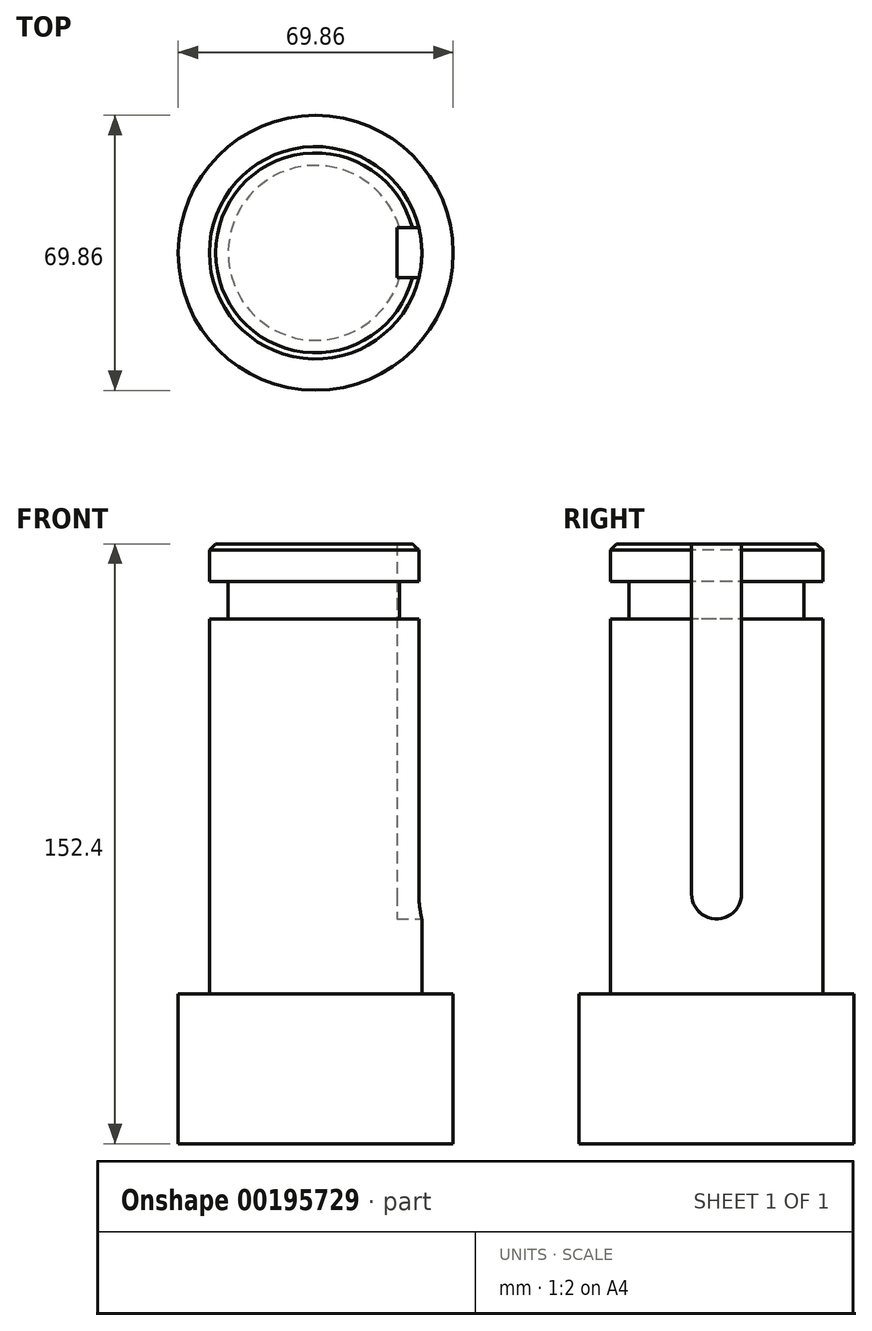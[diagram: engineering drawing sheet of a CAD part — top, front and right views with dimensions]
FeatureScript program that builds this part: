
annotation { "Feature Type Name" : "Feature", "Feature Type Description" : "" }
export const myFeature = defineFeature(function(context is Context, id is Id, definition is map)
    precondition{}
    {
        {
            var Q0;
            Q0=qCreatedBy(makeId("Top.planeOp"),FACE);
            var sketch = newSketch(context, id + "F0", { "sketchPlane" : qUnion([Q0])});
            skCircle(sketch, "E0", {"center": v(0, 0) * mm, "radius": 26.99 * mm});
            skSolve(sketch);
        }
        {
            var Q0;
            Q0 = qSketchRegion(id + "F0", true);
            extrude(context, id + "F1", {"entities" : qUnion([Q0]), "depth" : 133.35 * mm});
        }
        {
            var Q0;
            Q0=makeQuery(id+"F1.opExtrude","CAP_FACE",FACE,{"disambiguationData":[OSD([sQuery(id+"F0.wireOp",EDGE,"E0")])],"isStart":false});
            var sketch = newSketch(context, id + "F2", { "sketchPlane" : qUnion([Q0])});
            skCircle(sketch, "E1", {"center": v(0, 0) * mm, "radius": 22.23 * mm});
            skSolve(sketch);
        }
        {
            var Q0;
            Q0 = qSketchRegion(id + "F2", true);
            extrude(context, id + "F3", {"entities" : qUnion([Q0]), "operationType" : NewBodyOperationType.ADD, "depth" : 9.52 * mm});
        }
        {
            var Q0;
            Q0=makeQuery(id+"F3.opExtrude","CAP_FACE",FACE,{"disambiguationData":[OSD([sQuery(id+"F2.wireOp",EDGE,"E1")])],"isStart":false});
            var sketch = newSketch(context, id + "F4", { "sketchPlane" : qUnion([Q0])});
            skCircle(sketch, "E2", {"center": v(0, 0) * mm, "radius": 26.99 * mm});
            skSolve(sketch);
        }
        {
            var Q0;
            Q0 = qSketchRegion(id + "F4", true);
            extrude(context, id + "F5", {"entities" : qUnion([Q0]), "operationType" : NewBodyOperationType.ADD, "depth" : 9.52 * mm});
        }
        {
            var Q0;
            Q0=makeQuery(id+"F5.opExtrude","CAP_EDGE",EDGE,{"disambiguationData":[OSD([sQuery(id+"F4.wireOp",EDGE,"E2")])],"isStart":false});
            chamfer(context, id + "F6", {"entities" : qUnion([Q0]), "width" : 1.59 * mm, "tangentPropagation" : true});
        }
        {
            var Q0;
            Q0=qCreatedBy(makeId("Right.planeOp"),FACE);
            cPlane(context, id + "F7", {"entities" : qUnion([Q0]), "cplaneType" : CPlaneType.OFFSET, "offset" : 30.16 * mm, "width" : 152.4 * mm, "height" : 152.4 * mm});
        }
        {
            var Q0;
            Q0=qCreatedBy(id+"F7.planeOp",FACE);
            var sketch = newSketch(context, id + "F8", { "sketchPlane" : qUnion([Q0])});
            skLineSegment(sketch, "E3.bottom", {"start": v(6.35, 152.55) * mm, "end": v(-6.35, 152.55) * mm});
            skLineSegment(sketch, "E3.left", {"start": v(6.35, 152.55) * mm, "end": v(6.35, 63.44) * mm});
            skLineSegment(sketch, "E3.right", {"start": v(-6.35, 152.55) * mm, "end": v(-6.35, 63.44) * mm});
            skPoint(sketch, "E3.middle", {"position": v(0, 108) * mm});
            skArc(sketch, "E4", {"start": v(-6.35, 63.44) * mm, "mid": v(0, 57.09) * mm, "end": v(6.35, 63.44) * mm});
            skLineSegment(sketch, "E5", {"start": v(16.9, 57.15) * mm, "end": v(-36.23, 57.15) * mm, "construction": true});
            skLineSegment(sketch, "E6", {"start": v(0, 0) * mm, "end": v(0, 207.58) * mm, "construction": true});
            skSolve(sketch);
        }
        {
            var Q0;
            Q0 = qSketchRegion(id + "F8", true);
            extrude(context, id + "F9", {"entities" : qUnion([Q0]), "operationType" : NewBodyOperationType.REMOVE, "oppositeDirection" : true, "depth" : 9.52 * mm, "offsetDistance" : 25.4 * mm});
        }
        {
            var Q0;
            Q0=makeQuery(id+"F1.opExtrude","CAP_FACE",FACE,{"disambiguationData":[OSD([sQuery(id+"F0.wireOp",EDGE,"E0")])],"isStart":true});
            var sketch = newSketch(context, id + "F10", { "sketchPlane" : qUnion([Q0])});
            skCircle(sketch, "E7", {"center": v(0, 0) * mm, "radius": 34.93 * mm});
            skSolve(sketch);
        }
        {
            var Q0;
            Q0 = qSketchRegion(id + "F10", true);
            extrude(context, id + "F11", {"entities" : qUnion([Q0]), "operationType" : NewBodyOperationType.ADD, "oppositeDirection" : true, "depth" : 25.4 * mm});
        }
        {
            var Q0;
            Q0=makeQuery(id+"F11.opExtrude","CAP_FACE",FACE,{"disambiguationData":[OSD([sQuery(id+"F10.wireOp",EDGE,"E7")])],"isStart":false});
            extrude(context, id + "F12", {"entities" : qUnion([Q0]), "operationType" : NewBodyOperationType.ADD, "depth" : 12.7 * mm, "offsetDistance" : 25.4 * mm});
        }
    });
